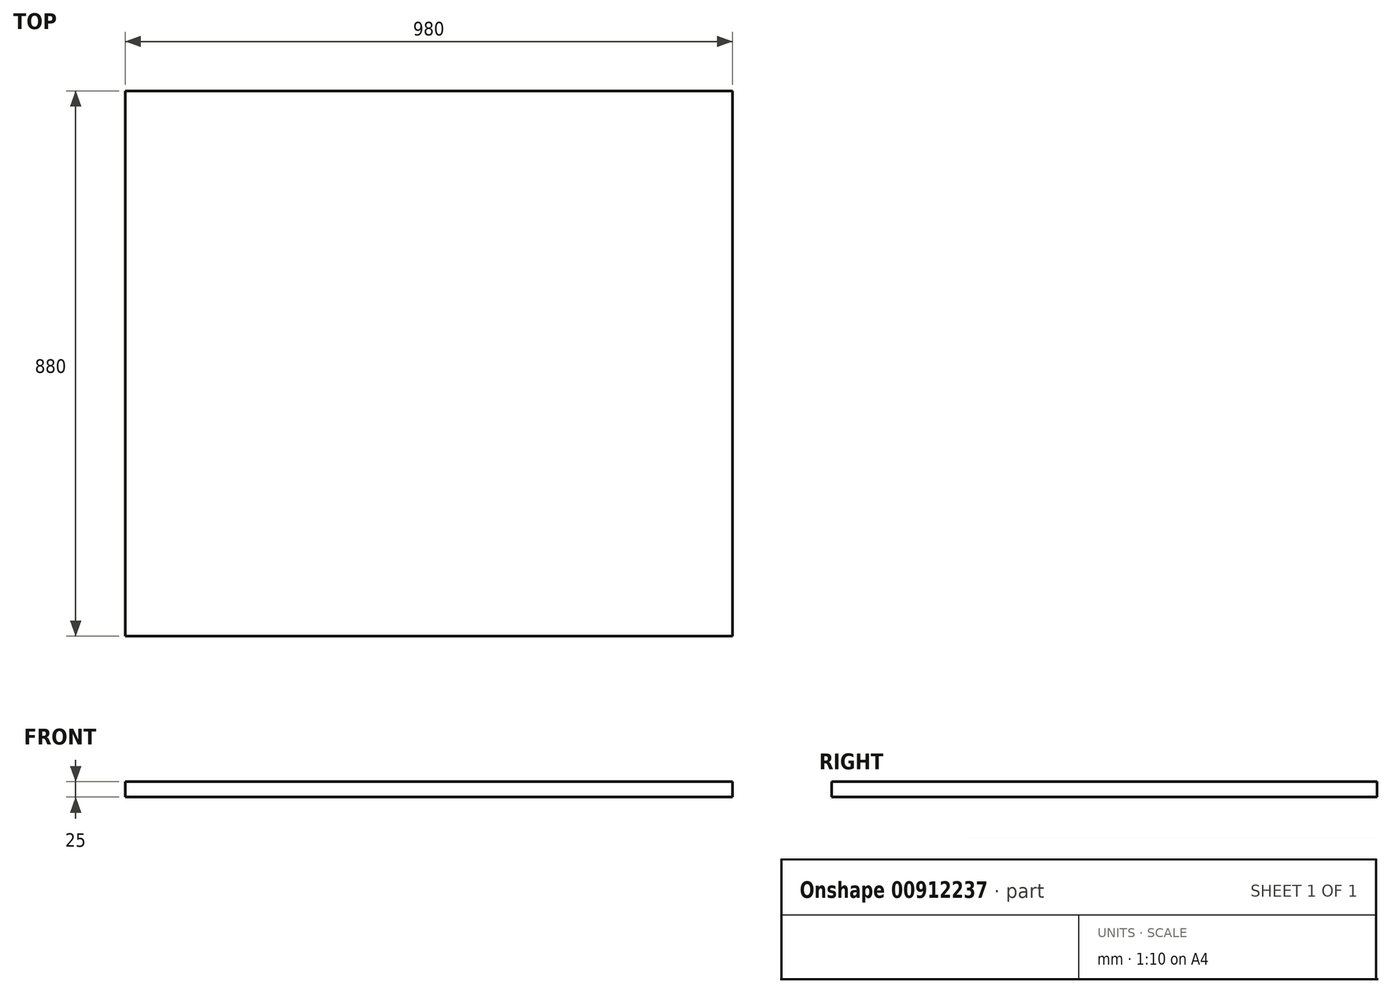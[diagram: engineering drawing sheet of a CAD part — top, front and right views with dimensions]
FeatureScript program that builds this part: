
annotation { "Feature Type Name" : "Feature", "Feature Type Description" : "" }
export const myFeature = defineFeature(function(context is Context, id is Id, definition is map)
    precondition{}
    {
        {
            var Q0;
            Q0=qCreatedBy(makeId("Top.planeOp"),FACE);
            var sketch = newSketch(context, id + "F0", { "sketchPlane" : qUnion([Q0])});
            skLineSegment(sketch, "E0.bottom", {"start": v(-39.59, 857.62) * mm, "end": v(940.41, 857.62) * mm});
            skLineSegment(sketch, "E0.top", {"start": v(-39.59, -22.38) * mm, "end": v(940.41, -22.38) * mm});
            skLineSegment(sketch, "E0.left", {"start": v(-39.59, 857.62) * mm, "end": v(-39.59, -22.38) * mm});
            skLineSegment(sketch, "E0.right", {"start": v(940.41, 857.62) * mm, "end": v(940.41, -22.38) * mm});
            skSolve(sketch);
        }
        {
            var Q0;
            Q0=qSketchRegion(id+"F0",true);
            extrude(context, id + "F1", {"entities" : qUnion([Q0]), "depth" : 25 * mm, "offsetDistance" : 25 * mm});
        }
    });
